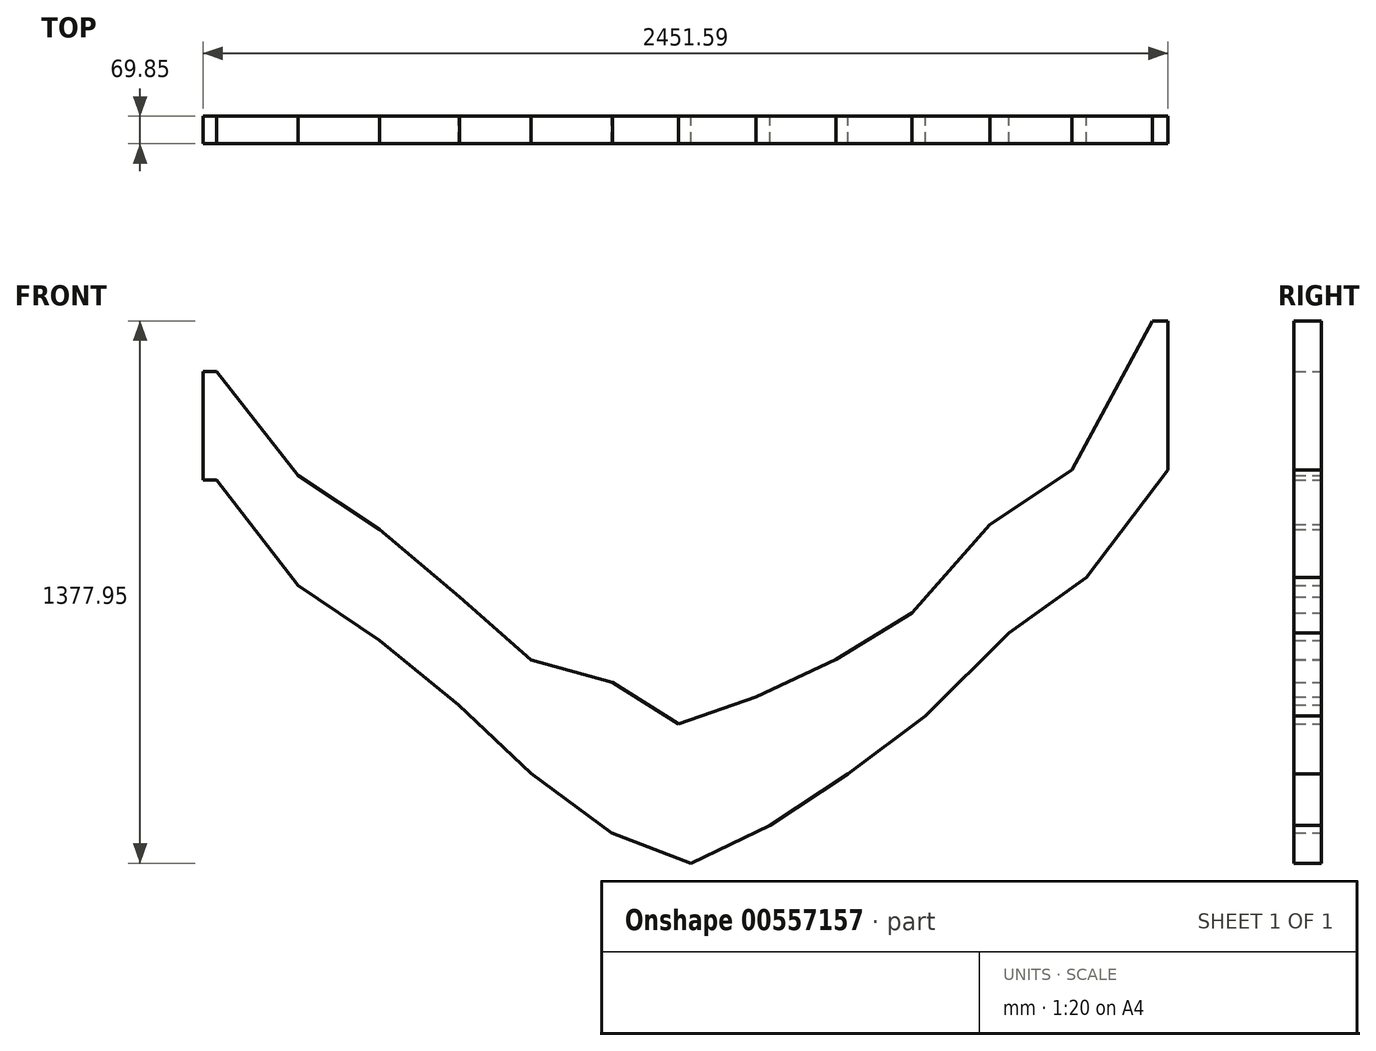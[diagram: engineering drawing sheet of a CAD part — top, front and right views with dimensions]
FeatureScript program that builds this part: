
annotation { "Feature Type Name" : "Feature", "Feature Type Description" : "" }
export const myFeature = defineFeature(function(context is Context, id is Id, definition is map)
    precondition{}
    {
        {
            var Q0;
            Q0=qCreatedBy(makeId("Front.planeOp"),FACE);
            var sketch = newSketch(context, id + "F0", { "sketchPlane" : qUnion([Q0])});
            skLineSegment(sketch, "E0", {"start": v(0, 0) * mm, "end": v(0, -275.44) * mm});
            skLineSegment(sketch, "E1", {"start": v(0, -275.44) * mm, "end": v(34.5, -275.44) * mm});
            skLineSegment(sketch, "E2", {"start": v(0, 0) * mm, "end": v(34.24, 0) * mm});
            skLineSegment(sketch, "E3", {"start": v(2451.59, 128.35) * mm, "end": v(2411.8, 128.35) * mm});
            skLineSegment(sketch, "E4", {"start": v(2451.59, 128.35) * mm, "end": v(2451.59, -250.93) * mm});
            skLineSegment(sketch, "E5", {"start": v(2451.59, -250.93) * mm, "end": v(2243.82, -524.12) * mm});
            skLineSegment(sketch, "E6", {"start": v(2243.82, -524.12) * mm, "end": v(2046.77, -664.77) * mm});
            skLineSegment(sketch, "E7", {"start": v(2046.77, -664.77) * mm, "end": v(1835.15, -875.79) * mm});
            skLineSegment(sketch, "E8", {"start": v(1835.15, -875.79) * mm, "end": v(1638.18, -1022.3) * mm});
            skLineSegment(sketch, "E9", {"start": v(1638.18, -1022.3) * mm, "end": v(1440.13, -1153.95) * mm});
            skLineSegment(sketch, "E10", {"start": v(1440.13, -1153.95) * mm, "end": v(1239.83, -1249.6) * mm});
            skLineSegment(sketch, "E11", {"start": v(1239.83, -1249.6) * mm, "end": v(1037.28, -1171.96) * mm});
            skLineSegment(sketch, "E12", {"start": v(1037.28, -1171.96) * mm, "end": v(832.63, -1021.44) * mm});
            skLineSegment(sketch, "E13", {"start": v(832.63, -1021.44) * mm, "end": v(649.42, -847) * mm});
            skLineSegment(sketch, "E14", {"start": v(649.42, -847) * mm, "end": v(448.5, -684.18) * mm});
            skLineSegment(sketch, "E15", {"start": v(448.5, -684.18) * mm, "end": v(240.65, -543.88) * mm});
            skLineSegment(sketch, "E16", {"start": v(240.65, -543.88) * mm, "end": v(34.5, -275.44) * mm});
            skLineSegment(sketch, "E17", {"start": v(34.24, 0) * mm, "end": v(240.65, -264.64) * mm});
            skLineSegment(sketch, "E18", {"start": v(240.65, -264.64) * mm, "end": v(448.6, -401.72) * mm});
            skLineSegment(sketch, "E19", {"start": v(448.6, -401.72) * mm, "end": v(651.1, -573.54) * mm});
            skLineSegment(sketch, "E20", {"start": v(651.1, -573.54) * mm, "end": v(832.63, -732.9) * mm});
            skLineSegment(sketch, "E21", {"start": v(832.63, -732.9) * mm, "end": v(1040.7, -790.58) * mm});
            skLineSegment(sketch, "E22", {"start": v(1040.7, -790.58) * mm, "end": v(1208.1, -895.9) * mm});
            skLineSegment(sketch, "E23", {"start": v(1208.1, -895.9) * mm, "end": v(1404, -827.15) * mm});
            skLineSegment(sketch, "E24", {"start": v(1404, -827.15) * mm, "end": v(1607.85, -731.66) * mm});
            skLineSegment(sketch, "E25", {"start": v(1607.85, -731.66) * mm, "end": v(1800.97, -613.64) * mm});
            skLineSegment(sketch, "E26", {"start": v(1800.97, -613.64) * mm, "end": v(1999.46, -389.4) * mm});
            skLineSegment(sketch, "E27", {"start": v(1999.46, -389.4) * mm, "end": v(2207.6, -250.93) * mm});
            skLineSegment(sketch, "E28", {"start": v(2207.6, -250.93) * mm, "end": v(2411.8, 128.35) * mm});
            skLineSegment(sketch, "E29", {"start": v(1239.83, -1249.6) * mm, "end": v(2467.78, -1249.6) * mm, "construction": true});
            skSolve(sketch);
        }
        {
            var Q0;
            Q0 = qSketchRegion(id + "F0", true);
            extrude(context, id + "F1", {"entities" : qUnion([Q0]), "depth" : 69.85 * mm, "offsetDistance" : 25.4 * mm});
        }
    });
